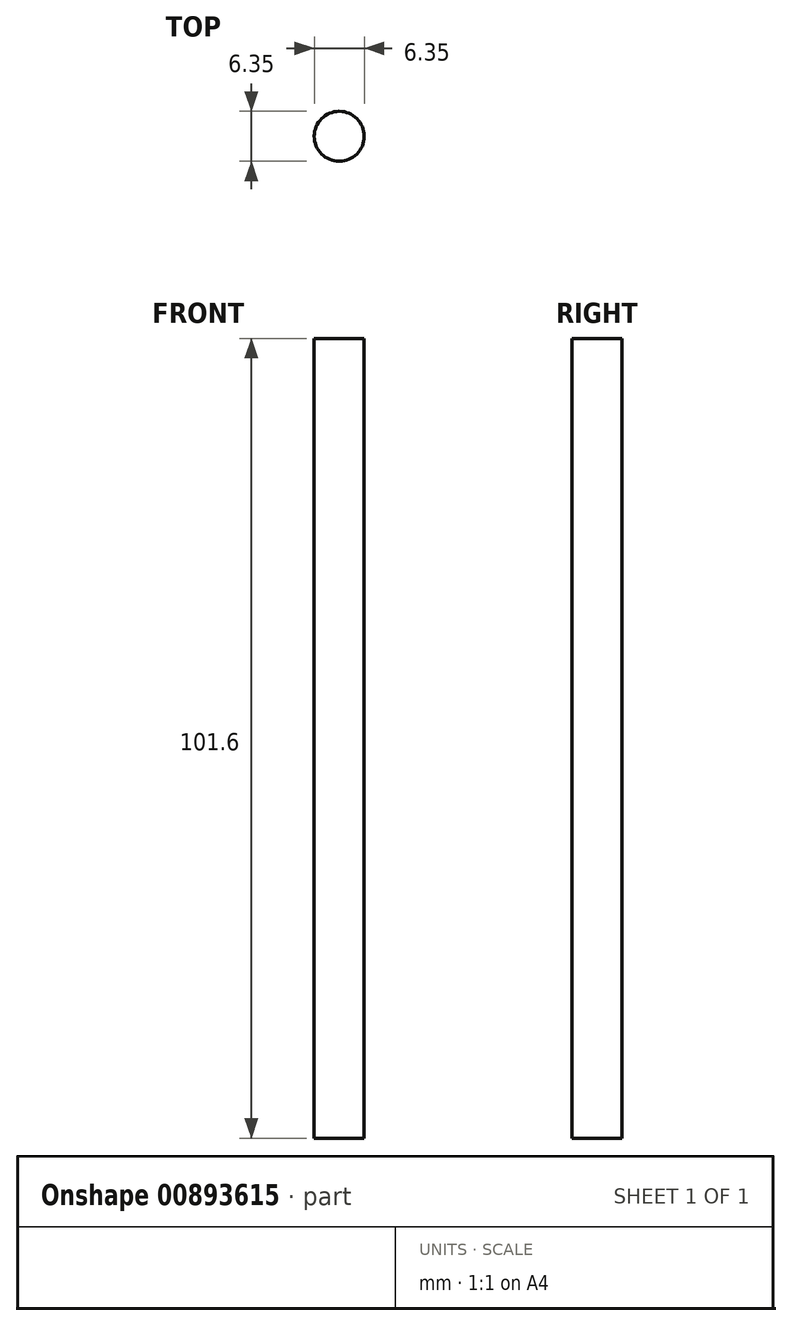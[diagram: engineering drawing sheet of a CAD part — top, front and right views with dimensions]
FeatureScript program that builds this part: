
annotation { "Feature Type Name" : "Feature", "Feature Type Description" : "" }
export const myFeature = defineFeature(function(context is Context, id is Id, definition is map)
    precondition{}
    {
        {
            var Q0;
            Q0=qCreatedBy(makeId("Top.planeOp"),FACE);
            var sketch = newSketch(context, id + "F0", { "sketchPlane" : qUnion([Q0])});
            skCircle(sketch, "E0", {"center": v(-3.7, 6.5) * mm, "radius": 3.18 * mm});
            skSolve(sketch);
        }
        {
            var Q0;
            Q0 = qSketchRegion(id + "F0", true);
            extrude(context, id + "F1", {"entities" : qUnion([Q0]), "depth" : 101.6 * mm, "offsetDistance" : 25.4 * mm});
        }
    });
